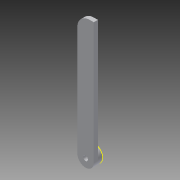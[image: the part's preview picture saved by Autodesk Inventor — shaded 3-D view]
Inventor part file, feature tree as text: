
AUTODESK INVENTOR PART (.ipt)
format: ipt  version: 2013 (Build 170138000, 138)  size: 361,472 bytes
history: native  units: in
note: dims shown in document units (in); Inventor stores cm internally (conversion verified against a paired STEP export)
features: sketch x7, extrude x6, fillet x1, pattern_circular x1
ambient origin geometry x8: Origin, YZ Plane, XZ Plane, XY Plane, X Axis, Y Axis, Z Axis, Center Point
bodies: Solid1 (feature_tree)
feature tree (15):
  extrude  "Extrusion1"  Depth=3.5in
  extrude  "Extrusion2"  Depth=0.4724in
  extrude  "Extrusion3"  Depth=0.2283in
  extrude  "Extrusion5"  Depth=0.0591in TaperAngle=0.0deg
  extrude  "Extrusion6"  Depth=0.0591in TaperAngle=0.0deg
  fillet  "Fillet2"  Radius=0.3543in
  sketch  "Sketch7"  dims[d24=0.1378in d25=0.0in d26=23.622in d27=360.0deg]
  extrude  "Extrusion7"  Depth=23.622in TaperAngle=360.0deg
  pattern_circular  "Circular Pattern2"  [2 undecoded]
  sketch  "Sketch1"  dims[d0=0.4724in d1=3.5in]
  sketch  "Sketch2"  dims[d2=0.1181in d3=0.0in d4=0.4724in]
  sketch  "Sketch3"  dims[d5=0.1378in d6=0.0in d7=0.2283in]
  sketch  "Sketch5"  dims[d8=0.1378in d9=0.0in d16=0.0591in d17=0.0in]
  sketch  "Sketch6"  dims[d18=0.1378in d19=0.0591in d20=0.0in d21=0.3543in]
  sketch  "Sketch8"
note: 2 required parameter values undecoded (feature->parameter linkage not recoverable at this tier; creation-order binding heuristic only, values carry confidence <= 0.55)
